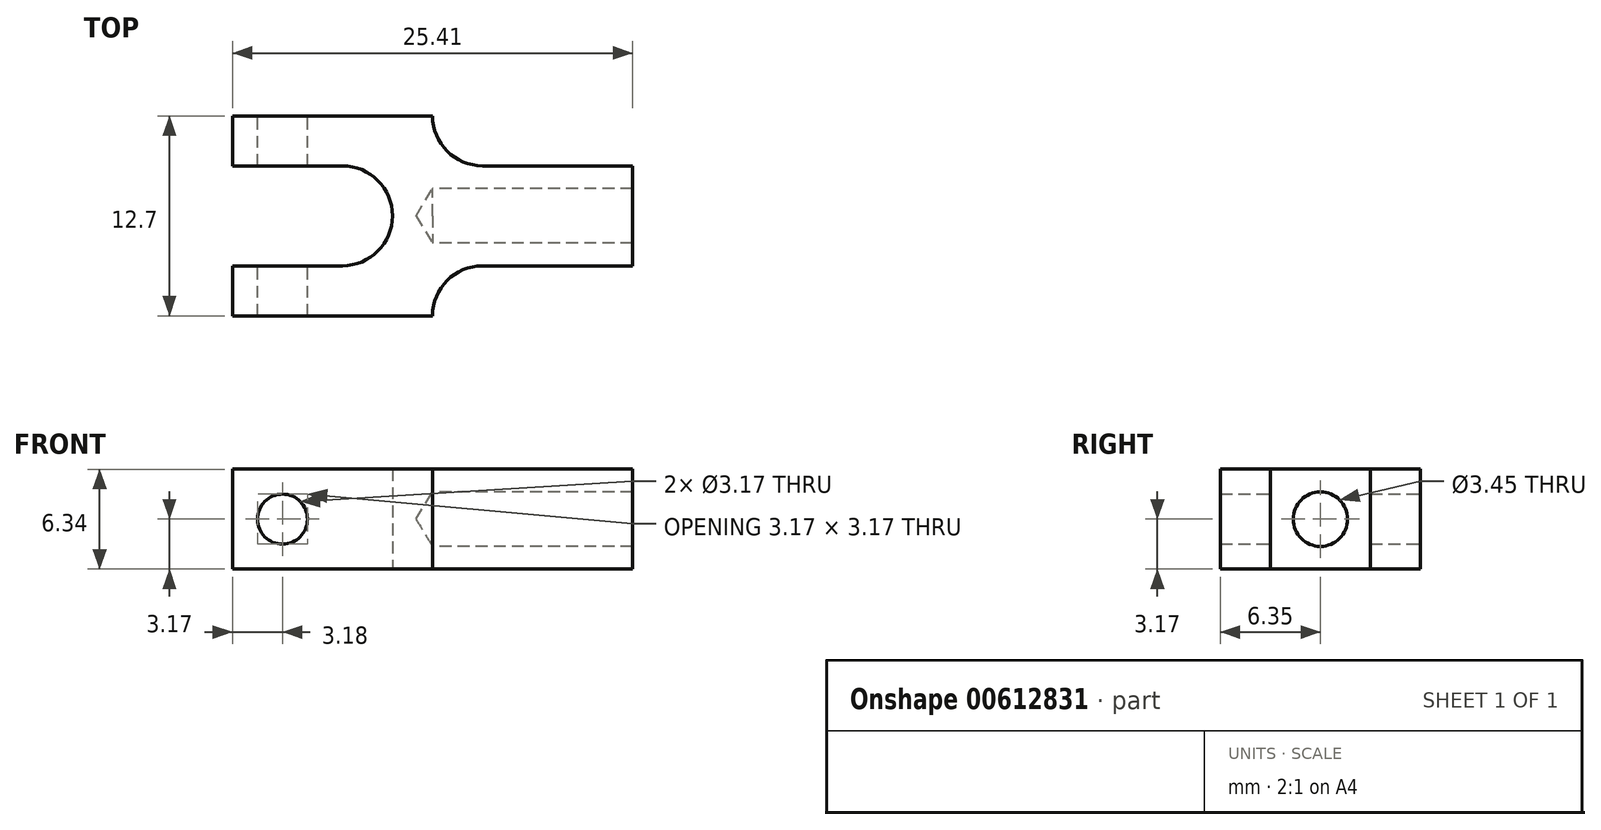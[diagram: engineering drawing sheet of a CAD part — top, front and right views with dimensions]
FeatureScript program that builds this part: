
annotation { "Feature Type Name" : "Feature", "Feature Type Description" : "" }
export const myFeature = defineFeature(function(context is Context, id is Id, definition is map)
    precondition{}
    {
        {
            var Q0;
            Q0=qCreatedBy(makeId("Top.planeOp"),FACE);
            var sketch = newSketch(context, id + "F0", { "sketchPlane" : qUnion([Q0])});
            skLineSegment(sketch, "E0", {"start": v(-6.98, -3.18) * mm, "end": v(-6.98, -6.35) * mm});
            skLineSegment(sketch, "E1", {"start": v(-6.99, -6.35) * mm, "end": v(5.72, -6.35) * mm});
            skArc(sketch, "E2", {"start": v(0, 3.18) * mm, "mid": v(3.18, 0) * mm, "end": v(0, -3.18) * mm});
            skLineSegment(sketch, "E3", {"start": v(0, -3.18) * mm, "end": v(-6.98, -3.18) * mm});
            skLineSegment(sketch, "E4", {"start": v(0, 3.18) * mm, "end": v(-6.98, 3.18) * mm});
            skLineSegment(sketch, "E5", {"start": v(-6.99, 3.18) * mm, "end": v(-6.99, 6.35) * mm});
            skLineSegment(sketch, "E6", {"start": v(-6.98, 6.35) * mm, "end": v(5.72, 6.35) * mm});
            skLineSegment(sketch, "E7", {"start": v(8.9, -3.18) * mm, "end": v(18.41, -3.18) * mm});
            skLineSegment(sketch, "E8", {"start": v(18.41, -3.18) * mm, "end": v(18.41, 3.18) * mm});
            skLineSegment(sketch, "E9", {"start": v(18.41, 3.18) * mm, "end": v(8.9, 3.18) * mm});
            skPoint(sketch, "E10", {"position": v(18.41, 0) * mm});
            skArc(sketch, "E11", {"start": v(8.9, 3.17) * mm, "mid": v(6.64, 4.1) * mm, "end": v(5.72, 6.35) * mm});
            skArc(sketch, "E12", {"start": v(8.9, -3.18) * mm, "mid": v(6.64, -4.1) * mm, "end": v(5.72, -6.35) * mm});
            skSolve(sketch);
        }
        {
            var Q0;
            Q0=qSketchRegion(id+"F0",true);
            extrude(context, id + "F1", {"entities" : qUnion([Q0]), "depth" : 6.35 * mm, "symmetric" : true});
        }
        {
            var Q0;
            Q0=makeQuery(id+"F1.opExtrude","SWEPT_FACE",FACE,{"disambiguationData":[OSD([sQuery(id+"F0.wireOp",EDGE,"E8")])]});
            var sketch = newSketch(context, id + "F2", { "sketchPlane" : qUnion([Q0])});
            skPoint(sketch, "E13", {"position": v(0, 0) * mm});
            skSolve(sketch);
        }
        {
            var Q0;
            Q0=sQuery(id+"F2.wireOp",VERTEX,"E13");
            var Q1;
            Q1=makeQuery(id+"F1.opExtrude","SWEPT_BODY",BODY,{"disambiguationData":[OSD([sQuery(id+"F0.wireOp",EDGE,"E0"),sQuery(id+"F0.wireOp",EDGE,"E1"),sQuery(id+"F0.wireOp",EDGE,"E2"),sQuery(id+"F0.wireOp",EDGE,"E3"),sQuery(id+"F0.wireOp",EDGE,"E4"),sQuery(id+"F0.wireOp",EDGE,"E5"),sQuery(id+"F0.wireOp",EDGE,"E6"),sQuery(id+"F0.wireOp",EDGE,"E7"),sQuery(id+"F0.wireOp",EDGE,"E8"),sQuery(id+"F0.wireOp",EDGE,"E9"),sQuery(id+"F0.wireOp",EDGE,"E11"),sQuery(id+"F0.wireOp",EDGE,"E12")])]});
            hole(context, id + "F3", {"style" : HoleStyle.SIMPLE, "holeDiameter" : 3.45 * mm, "endStyle" : HoleEndStyle.BLIND, "holeDepth" : 12.7 * mm, "locations" : qUnion([Q0]), "scope" : qUnion([Q1])});
        }
        {
            var Q0;
            Q0=makeQuery(id+"F1.opExtrude","SWEPT_FACE",FACE,{"disambiguationData":[OSD([sQuery(id+"F0.wireOp",EDGE,"E1")])]});
            var sketch = newSketch(context, id + "F4", { "sketchPlane" : qUnion([Q0])});
            skPoint(sketch, "E14", {"position": v(-3.81, 0) * mm});
            skSolve(sketch);
        }
        {
            var Q0;
            Q0=sQuery(id+"F4.wireOp",VERTEX,"E14");
            var Q1;
            Q1=makeQuery(id+"F1.opExtrude","SWEPT_BODY",BODY,{"disambiguationData":[OSD([sQuery(id+"F0.wireOp",EDGE,"E0"),sQuery(id+"F0.wireOp",EDGE,"E1"),sQuery(id+"F0.wireOp",EDGE,"E2"),sQuery(id+"F0.wireOp",EDGE,"E3"),sQuery(id+"F0.wireOp",EDGE,"E4"),sQuery(id+"F0.wireOp",EDGE,"E5"),sQuery(id+"F0.wireOp",EDGE,"E6"),sQuery(id+"F0.wireOp",EDGE,"E7"),sQuery(id+"F0.wireOp",EDGE,"E8"),sQuery(id+"F0.wireOp",EDGE,"E9"),sQuery(id+"F0.wireOp",EDGE,"E11"),sQuery(id+"F0.wireOp",EDGE,"E12")])]});
            hole(context, id + "F5", {"style" : HoleStyle.SIMPLE, "holeDiameter" : 3.17 * mm, "endStyle" : HoleEndStyle.THROUGH, "locations" : qUnion([Q0]), "scope" : qUnion([Q1])});
        }
    });
